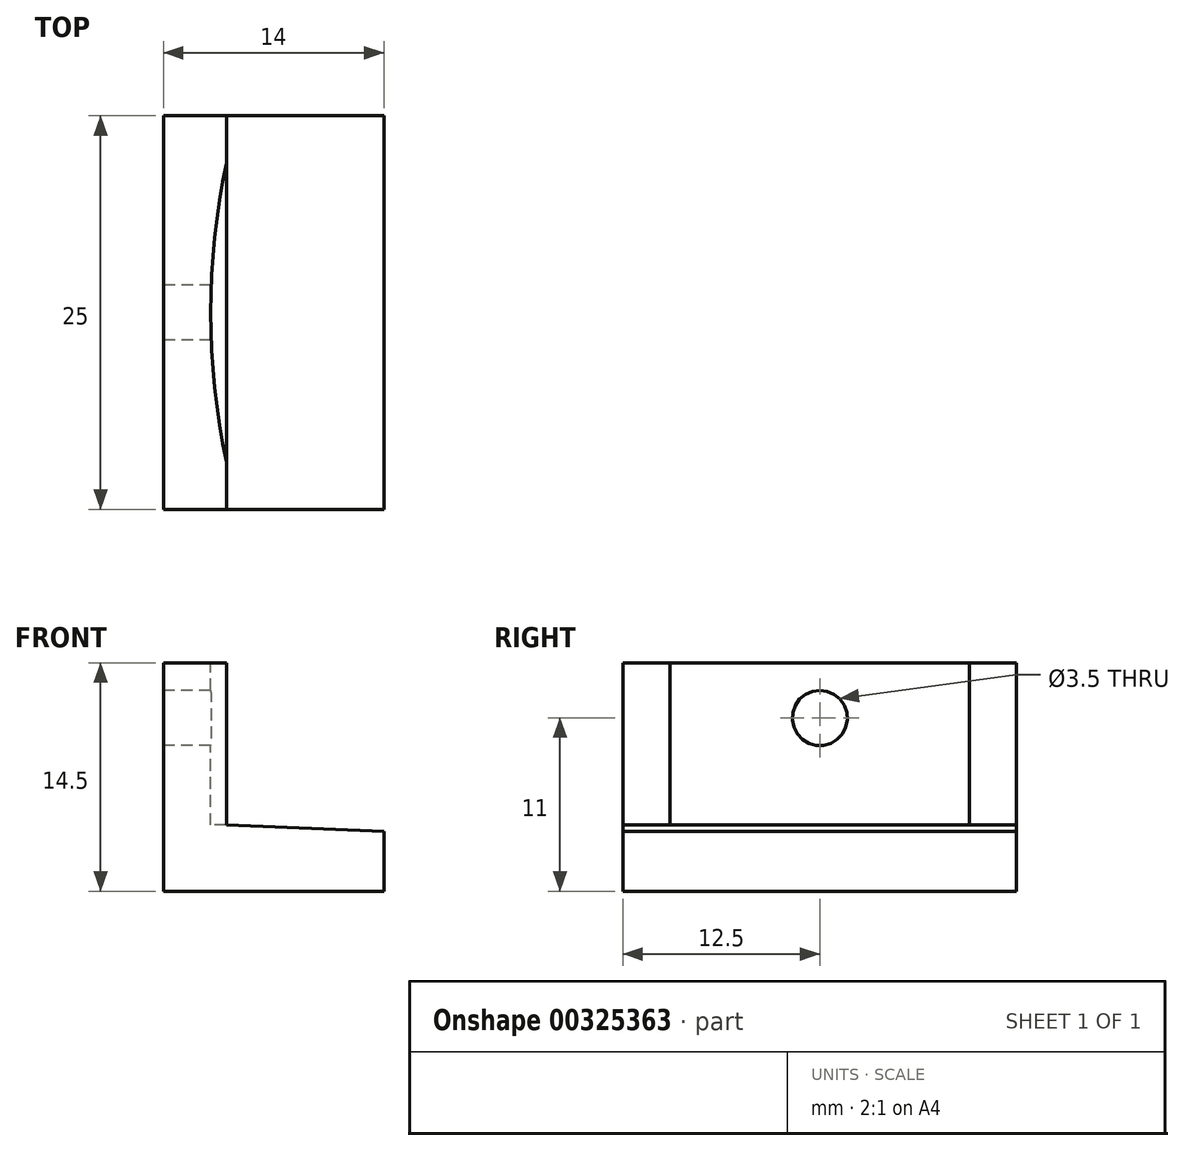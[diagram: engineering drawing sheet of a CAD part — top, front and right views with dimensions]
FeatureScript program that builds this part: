
annotation { "Feature Type Name" : "Feature", "Feature Type Description" : "" }
export const myFeature = defineFeature(function(context is Context, id is Id, definition is map)
    precondition{}
    {
        {
            var Q0;
            Q0=qCreatedBy(makeId("Front.planeOp"),FACE);
            var sketch = newSketch(context, id + "F0", { "sketchPlane" : qUnion([Q0])});
            skLineSegment(sketch, "E0", {"start": v(0, 0) * mm, "end": v(0, 14.5) * mm});
            skLineSegment(sketch, "E1", {"start": v(0, 14.5) * mm, "end": v(4, 14.5) * mm});
            skLineSegment(sketch, "E2", {"start": v(4, 14.5) * mm, "end": v(4, 4.2) * mm});
            skLineSegment(sketch, "E3", {"start": v(14, 3.8) * mm, "end": v(14, 0) * mm});
            skLineSegment(sketch, "E4", {"start": v(14, 0) * mm, "end": v(0, 0) * mm});
            skLineSegment(sketch, "E5", {"start": v(0, 7.5) * mm, "end": v(4, 7.5) * mm, "construction": true});
            skLineSegment(sketch, "E6", {"start": v(4, 4.2) * mm, "end": v(14, 3.8) * mm});
            skLineSegment(sketch, "E7", {"start": v(0, 4) * mm, "end": v(9, 4) * mm, "construction": true});
            skSolve(sketch);
        }
        {
            var Q0;
            Q0 = qSketchRegion(id + "F0", true);
            extrude(context, id + "F1", {"entities" : qUnion([Q0]), "depth" : 25 * mm});
        }
        {
            var Q0;
            Q0=makeQuery(id+"F1.opExtrude","SWEPT_FACE",FACE,{"disambiguationData":[OSD([sQuery(id+"F0.wireOp",EDGE,"E0")])]});
            var sketch = newSketch(context, id + "F2", { "sketchPlane" : qUnion([Q0])});
            skLineSegment(sketch, "E8", {"start": v(12.5, 14.5) * mm, "end": v(12.5, 0) * mm, "construction": true});
            skCircle(sketch, "E9", {"center": v(12.5, 11) * mm, "radius": 1.75 * mm});
            skSolve(sketch);
        }
        {
            var Q0;
            Q0 = qSketchRegion(id + "F2", true);
            extrude(context, id + "F3", {"entities" : qUnion([Q0]), "operationType" : NewBodyOperationType.REMOVE, "endBound" : BoundingType.THROUGH_ALL, "oppositeDirection" : true, "depth" : 25 * mm});
        }
        {
            var Q0;
            Q0=makeQuery(id+"F1.opExtrude","SWEPT_FACE",FACE,{"disambiguationData":[OSD([sQuery(id+"F0.wireOp",EDGE,"E1")])]});
            var sketch = newSketch(context, id + "F4", { "sketchPlane" : qUnion([Q0])});
            skLineSegment(sketch, "E10", {"start": v(4, 0) * mm, "end": v(4, -3) * mm, "construction": true});
            skLineSegment(sketch, "E11", {"start": v(4, -3) * mm, "end": v(4, -22) * mm});
            skLineSegment(sketch, "E12", {"start": v(4, -22) * mm, "end": v(4, -25) * mm, "construction": true});
            skArc(sketch, "E13", {"start": v(4, -3) * mm, "mid": v(3, -12.5) * mm, "end": v(4, -22) * mm});
            skSolve(sketch);
        }
        {
            var Q0;
            Q0 = qSketchRegion(id + "F4", true);
            var Q1;
            Q1=makeQuery(id+"F1.opExtrude","CAP_VERTEX",VERTEX,{"disambiguationData":[OSD([sQuery(id+"F0.wireOp",EDGE,"E2"),sQuery(id+"F0.wireOp",EDGE,"E6")])],"isStart":false});
            extrude(context, id + "F5", {"entities" : qUnion([Q0]), "operationType" : NewBodyOperationType.REMOVE, "endBound" : BoundingType.UP_TO_VERTEX, "oppositeDirection" : true, "endBoundEntityVertex" : qUnion([Q1]), "depth" : 25 * mm});
        }
    });
